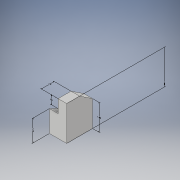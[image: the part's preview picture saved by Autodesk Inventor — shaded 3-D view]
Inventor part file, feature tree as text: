
AUTODESK INVENTOR PART (.ipt)
format: ipt  version: 2018 (Build 220112000, 112)  size: 123,392 bytes
history: native  units: in
note: dims shown in document units (in); Inventor stores cm internally (conversion verified against a paired STEP export)
features: other x6, sketch x2, extrude x1, draft x1, chamfer x1
ambient origin geometry x8: Origin, YZ Plane, XZ Plane, XY Plane, X Axis, Y Axis, Z Axis, Center Point
bodies: Solid1 (feature_tree)
feature tree (11):
  other  "Annotations"
  sketch  "Sketch1"  dims[d0=0.5in d1=2.0in]
  extrude  "Extrusion1"  Depth=2.0in
  draft  "FaceDraft2"
  chamfer  "Chamfer1"  Distance=1.25in
  sketch  "Sketch2"  dims[d2=1.0in d3=1.25in d4=1.5in d5=0.0in d13=0.1821in d25=0.75in d26=0.125in d27=0.2309in d10=0.0in d11=0.3937in d12=2.0in d14=0.0in d15=0.3937in d16=0.5021in d17=0.0in d18=0.3937in d19=1.25in d28=0.0in d29=0.3937in d30=1.5017in d31=0.0in d32=0.3937in d33=0.75in]
  other  "Linear Dimension 2"
  other  "Linear Dimension 3"
  other  "Linear Dimension 4"
  other  "Linear Dimension 5"
  other  "Linear Dimension 6"
